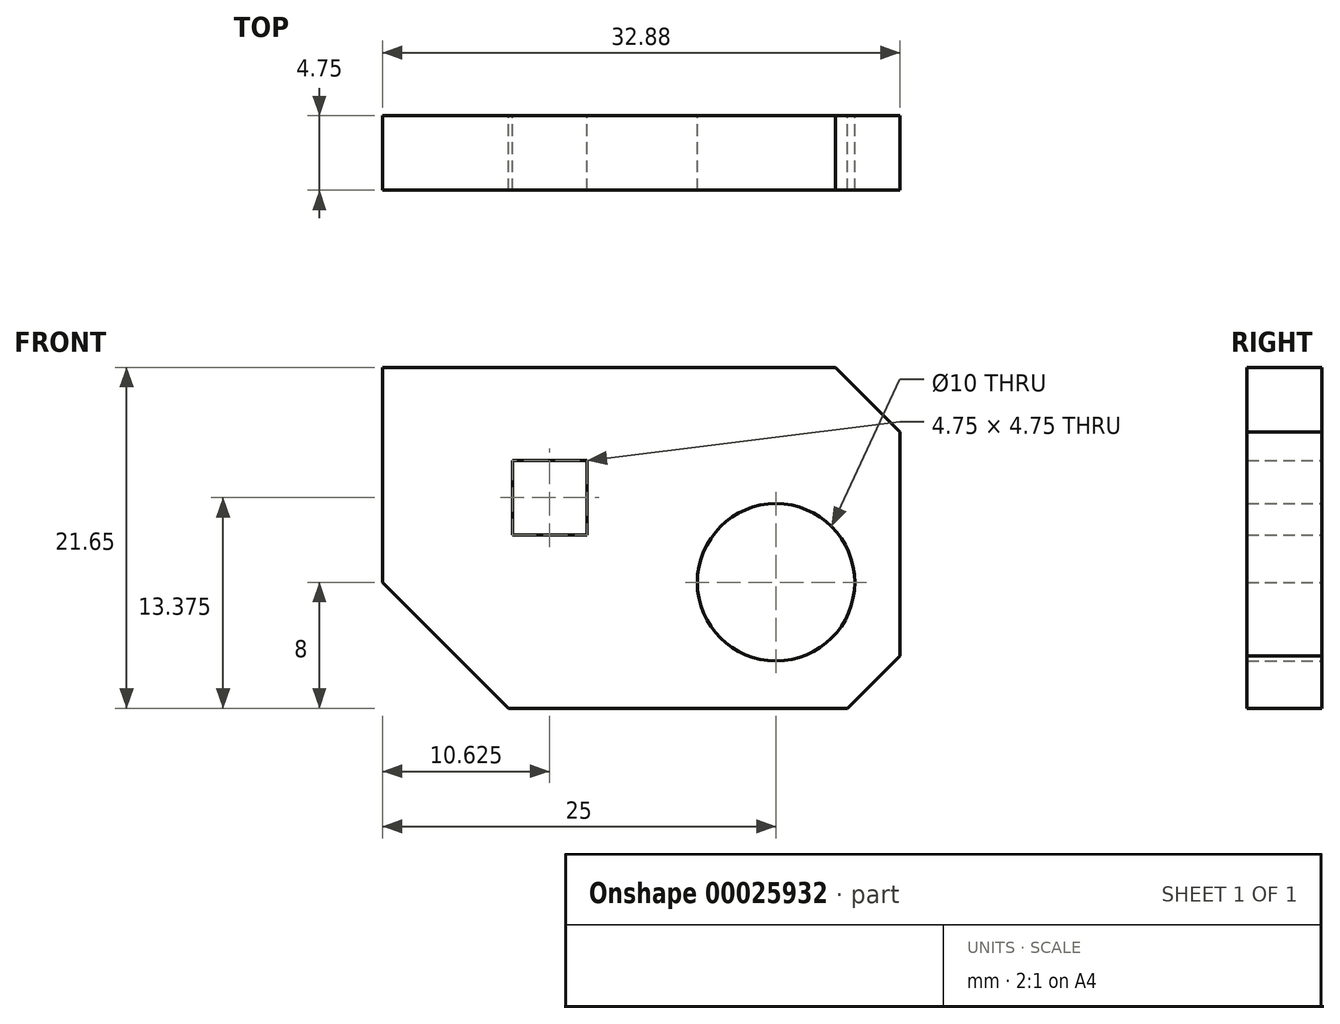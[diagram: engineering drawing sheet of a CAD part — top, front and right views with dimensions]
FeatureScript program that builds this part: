
annotation { "Feature Type Name" : "Feature", "Feature Type Description" : "" }
export const myFeature = defineFeature(function(context is Context, id is Id, definition is map)
    precondition{}
    {
        {
            var Q0;
            Q0=qCreatedBy(makeId("Front.planeOp"),FACE);
            var sketch = newSketch(context, id + "F0", { "sketchPlane" : qUnion([Q0])});
            skLineSegment(sketch, "E0.bottom", {"start": v(0, 0) * mm, "end": v(66.5, 0) * mm, "construction": true});
            skLineSegment(sketch, "E0.top", {"start": v(0, 38) * mm, "end": v(66.5, 38) * mm, "construction": true});
            skLineSegment(sketch, "E0.left", {"start": v(0, 0) * mm, "end": v(0, 23.25) * mm, "construction": true});
            skLineSegment(sketch, "E0.right", {"start": v(66.5, 0) * mm, "end": v(66.5, 38) * mm, "construction": true});
            skLineSegment(sketch, "E1", {"start": v(-4, -8) * mm, "end": v(48.64, -8) * mm, "construction": true});
            skLineSegment(sketch, "E2", {"start": v(48.64, -8) * mm, "end": v(52.64, -4) * mm, "construction": true});
            skLineSegment(sketch, "E3", {"start": v(52.64, -4) * mm, "end": v(102.5, -4) * mm, "construction": true});
            skLineSegment(sketch, "E4", {"start": v(102.5, -4) * mm, "end": v(110.5, -12) * mm});
            skLineSegment(sketch, "E5", {"start": v(110.5, -12) * mm, "end": v(132.04, -12) * mm});
            skLineSegment(sketch, "E6", {"start": v(70.39, 50) * mm, "end": v(-4, 50) * mm, "construction": true});
            skArc(sketch, "E7", {"start": v(-4, 50) * mm, "mid": v(-8.51, 47.97) * mm, "end": v(-10, 43.26) * mm, "construction": true});
            skLineSegment(sketch, "E8", {"start": v(-10, 43.26) * mm, "end": v(-4, -8) * mm, "construction": true});
            skCircle(sketch, "E9", {"center": v(127.5, -4) * mm, "radius": 5 * mm});
            skLineSegment(sketch, "E10", {"start": v(70.39, 50) * mm, "end": v(73.77, 46.62) * mm, "construction": true});
            skLineSegment(sketch, "E11", {"start": v(73.77, 46.62) * mm, "end": v(73.77, 0) * mm, "construction": true});
            skLineSegment(sketch, "E12", {"start": v(73.77, 0) * mm, "end": v(102.5, 0) * mm, "construction": true});
            skLineSegment(sketch, "E13", {"start": v(102.5, 0) * mm, "end": v(102.5, 9.65) * mm});
            skLineSegment(sketch, "E14", {"start": v(102.5, 9.65) * mm, "end": v(131.28, 9.65) * mm});
            skLineSegment(sketch, "E15", {"start": v(131.28, 9.65) * mm, "end": v(135.38, 5.55) * mm});
            skLineSegment(sketch, "E16", {"start": v(135.38, 5.55) * mm, "end": v(135.38, -8.67) * mm});
            skLineSegment(sketch, "E17", {"start": v(135.38, -8.67) * mm, "end": v(132.04, -12) * mm});
            skLineSegment(sketch, "E18.bottom", {"start": v(-1.5, 38) * mm, "end": v(-6.25, 38) * mm, "construction": true});
            skLineSegment(sketch, "E18.top", {"start": v(-1.5, 33.25) * mm, "end": v(-6.25, 33.25) * mm, "construction": true});
            skLineSegment(sketch, "E18.left", {"start": v(-1.5, 38) * mm, "end": v(-1.5, 33.25) * mm, "construction": true});
            skLineSegment(sketch, "E18.right", {"start": v(-6.25, 38) * mm, "end": v(-6.25, 33.25) * mm, "construction": true});
            skLineSegment(sketch, "E19.bottom", {"start": v(110.75, 3.75) * mm, "end": v(115.5, 3.75) * mm});
            skLineSegment(sketch, "E19.top", {"start": v(110.75, -1) * mm, "end": v(115.5, -1) * mm});
            skLineSegment(sketch, "E19.left", {"start": v(110.75, 3.75) * mm, "end": v(110.75, -1) * mm});
            skLineSegment(sketch, "E19.right", {"start": v(115.5, 3.75) * mm, "end": v(115.5, -1) * mm});
            skLineSegment(sketch, "E20", {"start": v(0, 28) * mm, "end": v(-4.75, 28) * mm, "construction": true});
            skLineSegment(sketch, "E21", {"start": v(-4.75, 28) * mm, "end": v(-4.75, 23.25) * mm, "construction": true});
            skLineSegment(sketch, "E22", {"start": v(-4.75, 23.25) * mm, "end": v(0, 23.25) * mm, "construction": true});
            skLineSegment(sketch, "E23.trimOffspring", {"start": v(0, 28) * mm, "end": v(0, 38) * mm, "construction": true});
            skLineSegment(sketch, "E24", {"start": v(102.5, 0) * mm, "end": v(86.5, 0) * mm, "construction": true});
            skLineSegment(sketch, "E25", {"start": v(86.5, 0) * mm, "end": v(86.5, -4) * mm, "construction": true});
            skLineSegment(sketch, "E26", {"start": v(86.5, -4) * mm, "end": v(102.5, -4) * mm, "construction": true});
            skLineSegment(sketch, "E27", {"start": v(102.5, 0) * mm, "end": v(102.5, -4) * mm});
            skSolve(sketch);
        }
        {
            var Q0;
            Q0=qSketchRegion(id+"F0",true);
            extrude(context, id + "F1", {"entities" : qUnion([Q0]), "depth" : 4.75 * mm});
        }
    });
